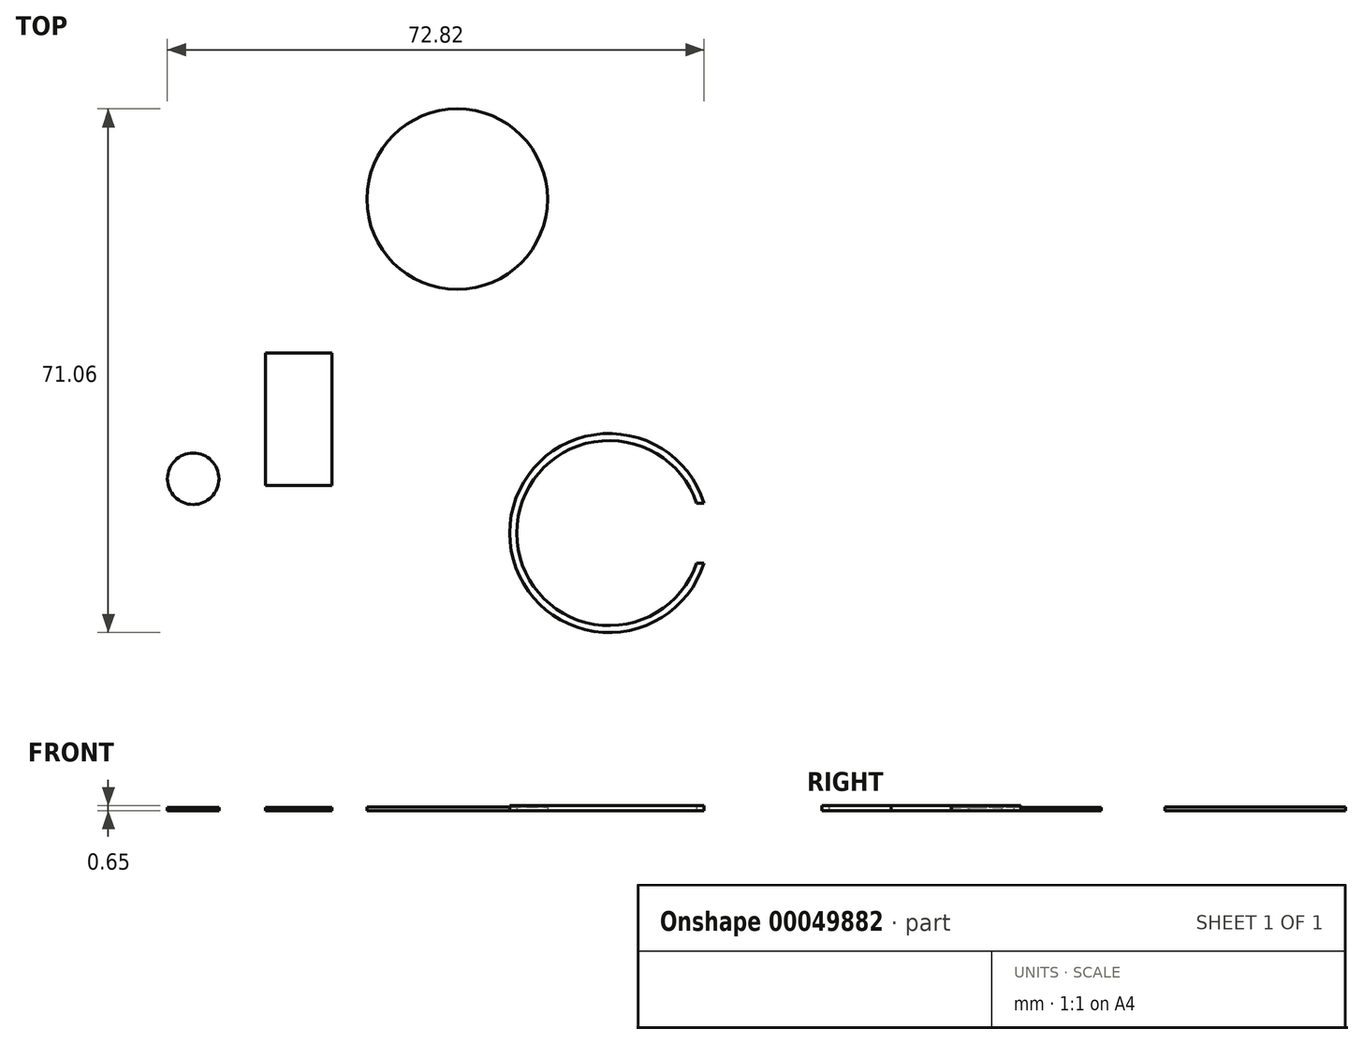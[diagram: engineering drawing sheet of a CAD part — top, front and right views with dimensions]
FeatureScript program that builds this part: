
annotation { "Feature Type Name" : "Feature", "Feature Type Description" : "" }
export const myFeature = defineFeature(function(context is Context, id is Id, definition is map)
    precondition{}
    {
        {
            var Q0;
            Q0=qCreatedBy(makeId("Top.planeOp"),FACE);
            var sketch = newSketch(context, id + "F0", { "sketchPlane" : qUnion([Q0])});
            skCircle(sketch, "E0", {"center": v(-23.37, 19.1) * mm, "radius": 3.5 * mm});
            skLineSegment(sketch, "E1.bottom", {"start": v(-13.56, 36.17) * mm, "end": v(-4.56, 36.17) * mm});
            skLineSegment(sketch, "E1.top", {"start": v(-13.56, 18.17) * mm, "end": v(-4.56, 18.17) * mm});
            skLineSegment(sketch, "E1.left", {"start": v(-13.56, 36.17) * mm, "end": v(-13.56, 18.17) * mm});
            skLineSegment(sketch, "E1.right", {"start": v(-4.56, 36.17) * mm, "end": v(-4.56, 18.17) * mm});
            skCircle(sketch, "E2", {"center": v(33.08, 11.74) * mm, "radius": 12.55 * mm});
            skCircle(sketch, "E3", {"center": v(33.08, 11.74) * mm, "radius": 13.5 * mm});
            skLineSegment(sketch, "E4.bottom", {"start": v(44.08, 15.81) * mm, "end": v(47.08, 15.81) * mm});
            skLineSegment(sketch, "E4.top", {"start": v(44.08, 7.66) * mm, "end": v(47.08, 7.66) * mm});
            skPoint(sketch, "E5.visualSharp", {"position": v(47.08, 15.81) * mm});
            skPoint(sketch, "E6.visualSharp", {"position": v(47.08, 7.66) * mm});
            skPoint(sketch, "E7.visualSharp", {"position": v(44.08, 7.66) * mm});
            skPoint(sketch, "E8.visualSharp", {"position": v(44.08, 15.81) * mm});
            skLineSegment(sketch, "E9", {"start": v(47.08, 15.81) * mm, "end": v(47.08, 7.66) * mm});
            skLineSegment(sketch, "E10", {"start": v(44.08, 7.66) * mm, "end": v(44.08, 15.81) * mm});
            skCircle(sketch, "E11", {"center": v(12.46, 57.05) * mm, "radius": 12.25 * mm});
            skSolve(sketch);
        }
        {
            var Q0;
            Q0=makeQuery(id+"F0.imprint","IMPRINT",FACE,{"disambiguationData":[TD([[makeQuery(id+"F0.imprint","IMPRINT",EDGE,{"derivedFrom":sQuery(id+"F0.wireOp",EDGE,"E0")}),1.0]])]});
            extrude(context, id + "F1", {"entities" : qUnion([Q0]), "depth" : .4 * mm});
        }
        {
            var Q0;
            Q0=makeQuery(id+"F0.imprint","IMPRINT",FACE,{"disambiguationData":[TD([[makeQuery(id+"F0.imprint","IMPRINT",EDGE,{"derivedFrom":sQuery(id+"F0.wireOp",EDGE,"E1.bottom")}),-1.0]])]});
            extrude(context, id + "F2", {"entities" : qUnion([Q0]), "depth" : .4 * mm});
        }
        {
            var Q0;
            {var subQ1=sQuery(id+"F0.wireOp",EDGE,"E2");var subQ5=sQuery(id+"F0.wireOp",EDGE,"E4.bottom");var subQ6=makeQuery(id+"F0.imprint","INTERSECT",VERTEX,{"derivedFrom":[subQ1,subQ5]});Q0=makeQuery(id+"F0.imprint","IMPRINT",FACE,{"disambiguationData":[TD([[makeQuery(id+"F0.imprint","IMPRINT",EDGE,{"disambiguationData":[TD([[subQ6,-1.0]])],"derivedFrom":subQ1}),-1.0]])]});}
            extrude(context, id + "F3", {"entities" : qUnion([Q0]), "depth" : .65 * mm});
        }
        {
            var Q0;
            Q0=makeQuery(id+"F0.imprint","IMPRINT",FACE,{"disambiguationData":[TD([[makeQuery(id+"F0.imprint","IMPRINT",EDGE,{"derivedFrom":sQuery(id+"F0.wireOp",EDGE,"E11")}),1.0]])]});
            extrude(context, id + "F4", {"entities" : qUnion([Q0]), "depth" : .5 * mm});
        }
    });
